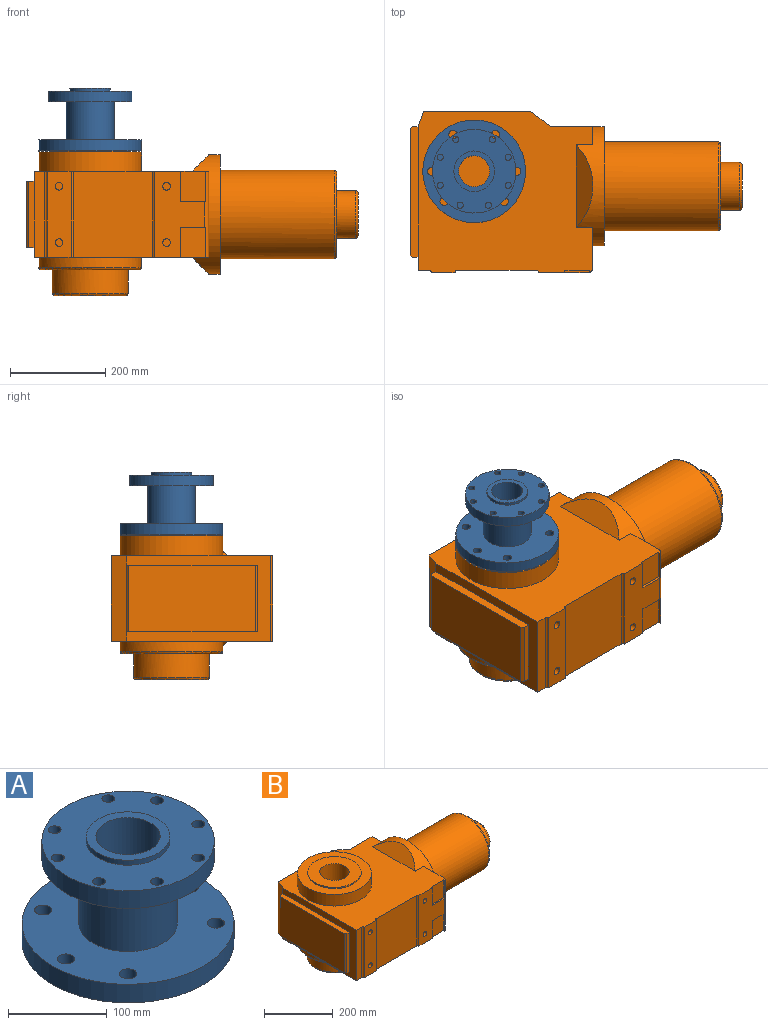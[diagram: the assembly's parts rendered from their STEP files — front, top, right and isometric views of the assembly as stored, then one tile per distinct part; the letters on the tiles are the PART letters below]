
ASSEMBLY  parts=2 mates=1
PART A: 26 faces, bbox 215x215x131 mm
  f0: plane 215x215mm, normal (0,0,-1), area 16235.4mm2, adj f1,f10,f20,f21,f22,f23,f24,f25
  f1: cylinder r=107.5mm len=215mm, axis (0,0,-1), area 15535.2mm2, adj f0,f2
  f2: plane 215x215mm, normal (0,0,1), area 27007.9mm2, adj f1,f3,f20,f21,f22,f23,f24,f25
  f3: cylinder r=50mm len=100mm, axis (0,0,-1), area 25132.7mm2, adj f2,f6
  f4: cylinder r=87.5mm len=175mm, axis (0,0,-1), area 12095.1mm2, adj f5,f6
  f5: plane 175x175mm, normal (0,0,1), area 17316.5mm2, adj f4,f8,f12,f13,f14,f15,f16,f17
  f6: plane 175x175mm, normal (0,0,-1), area 15137mm2, adj f3,f4,f12,f13,f14,f15,f16,f17
  f7: cylinder r=32.5mm len=125mm, axis (0,0,-1), area 25525.4mm2, adj f9,f11
  f8: cylinder r=42.5mm len=85mm, axis (0,0,-1), area 1602.2mm2, adj f5,f9
  f9: plane 85x85mm, normal (0,0,1), area 2356.2mm2, adj f7,f8
  f10: cylinder r=77mm len=154mm, axis (0,0,-1), area 2902.8mm2, adj f0,f11
  f11: plane 154x154mm, normal (0,0,-1), area 15308.2mm2, adj f7,f10
  f12: cylinder r=6.5mm len=22mm, axis (0,0,1), area 898.5mm2, adj f5,f6
  f13: cylinder r=6.5mm len=22mm, axis (0,0,1), area 898.5mm2, adj f5,f6
  f14: cylinder r=6.5mm len=22mm, axis (0,0,1), area 898.5mm2, adj f5,f6
  f15: cylinder r=6.5mm len=22mm, axis (0,0,1), area 898.5mm2, adj f5,f6
  f16: cylinder r=6.5mm len=22mm, axis (0,0,1), area 898.5mm2, adj f5,f6
  f17: cylinder r=6.5mm len=22mm, axis (0,0,1), area 898.5mm2, adj f5,f6
  f18: cylinder r=6.5mm len=22mm, axis (0,0,1), area 898.5mm2, adj f5,f6
  f19: cylinder r=6.5mm len=22mm, axis (0,0,1), area 898.5mm2, adj f5,f6
  f20: cylinder r=8.75mm len=23mm, axis (0,0,-1), area 1264.5mm2, adj f0,f2
  f21: cylinder r=8.75mm len=23mm, axis (0,0,-1), area 1264.5mm2, adj f0,f2
  f22: cylinder r=8.75mm len=23mm, axis (0,0,-1), area 1264.5mm2, adj f0,f2
  f23: cylinder r=8.75mm len=23mm, axis (0,0,-1), area 1264.5mm2, adj f0,f2
  f24: cylinder r=8.75mm len=23mm, axis (0,0,-1), area 1264.5mm2, adj f0,f2
  f25: cylinder r=8.75mm len=23mm, axis (0,0,-1), area 1264.5mm2, adj f0,f2
PART B: 64 faces, bbox 695.5x338x305 mm
  f0: plane 180x84.25mm, normal (1,0,0), area 10413.4mm2, adj f2,f4,f24,f38
  f1: plane 90x38.25mm, normal (1,0,0), area 1066.7mm2, adj f4,f35,f38
  f2: plane 366x338mm, normal (0,0,1), area 76361mm2, adj f0,f3,f5,f6,f7,f8,f9,f11
  f3: plane 224.35x180mm, normal (0,1,0), area 40383mm2, adj f2,f4,f32,f34
  f4: plane 366x338mm, normal (0,0,-1), area 76361mm2, adj f0,f1,f3,f5,f6,f7,f11,f12
  f5: plane 180x103.5mm, normal (0,-1,0), area 12116.9mm2, adj f2,f4,f14,f15,f18,f19,f21,f24
  f6: plane 300.95x180mm, normal (-1,0,0), area 16092mm2, adj f2,f4,f12,f26,f27,f28,f32
  f7: plane 180x50mm, normal (0,-1,0), area 8597.9mm2, adj f2,f4,f22,f23,f48,f50
  f8: plane 90x38.25mm, normal (1,0,0), area 1066.7mm2, adj f2,f35,f38
  f9: cylinder r=107.5mm len=215mm, axis (0,0,-1), area 27693.1mm2, adj f2,f10
  f10: plane 215x215mm, normal (0,0,1), area 17435.8mm2, adj f9,f60
  f11: plane 180x165mm, normal (0,-1,0), area 29700mm2, adj f2,f4,f21,f22
  f12: plane 180x22.5mm, normal (0,-1,0), area 4050mm2, adj f2,f4,f6,f23
  f13: plane 63x4.47mm, normal (-1,0,0), area 281.9mm2, adj f4,f14,f16,f24
  f14: plane 51.7x5mm, normal (0,0,-1), area 257.9mm2, adj f5,f13,f15,f16,f24
  f15: plane 63x5mm, normal (1,0,0), area 315mm2, adj f4,f5,f14,f16
  f16: plane 63x51.7mm, normal (0,-1,0), area 3257.1mm2, adj f4,f13,f14,f15
  f17: plane 63x4.47mm, normal (-1,0,0), area 281.9mm2, adj f2,f19,f20,f24
  f18: plane 63x5mm, normal (1,0,0), area 315mm2, adj f2,f5,f19,f20
  f19: plane 51.7x5mm, normal (0,0,1), area 257.9mm2, adj f5,f17,f18,f20,f24
  f20: plane 63x51.7mm, normal (0,-1,0), area 3257.1mm2, adj f2,f17,f18,f19
  f21: cylinder r=5mm len=180mm, axis (0,0,-1), area 1413.7mm2, adj f2,f4,f5,f11
  f22: cylinder r=5mm len=180mm, axis (0,0,-1), area 1413.7mm2, adj f2,f4,f7,f11
  f23: cylinder r=5mm len=180mm, axis (0,0,-1), area 1413.7mm2, adj f2,f4,f7,f12
  f24: cylinder r=10mm len=180mm, axis (0,0,-1), area 2417mm2, adj f0,f2,f4,f5,f13,f14,f17,f19
  f25: plane 139x12mm, normal (0,1,0), area 1668mm2, adj f26,f28,f33,f36
  f26: plane 274x17mm, normal (0,0,-1), area 4633mm2, adj f6,f25,f27,f29,f33,f36,f37
  f27: plane 139x12mm, normal (0,-1,0), area 1668mm2, adj f6,f26,f28,f37
  f28: plane 274x17mm, normal (0,0,1), area 4633mm2, adj f6,f25,f27,f29,f33,f36,f37
  f29: plane 264x139mm, normal (-1,0,0), area 36696mm2, adj f26,f28,f36,f37
  f30: cylinder r=107.5mm len=215mm, axis (0,0,1), area 14184.3mm2, adj f4,f59
  f31: plane 205x205mm, normal (0,0,-1), area 13150.7mm2, adj f57,f59
  f32: plane 180x32.05mm, normal (-0.94,0.34,0), area 6138.1mm2, adj f2,f3,f4,f6,f33
  f33: plane 139x0.05mm, normal (1,0,0), area 6.8mm2, adj f25,f26,f28,f32
  f34: plane 180x40.8mm, normal (0.62,0.79,0), area 9333.4mm2, adj f2,f3,f4,f35
  f35: plane 180x89.2mm, normal (0,1,0), area 16056mm2, adj f1,f2,f4,f8,f34
  f36: plane 139x5mm, normal (-0.71,0.71,0), area 982.9mm2, adj f25,f26,f28,f29
  f37: plane 139x5mm, normal (-0.71,-0.71,0), area 982.9mm2, adj f26,f27,f28,f29
  f38: cylinder r=125mm len=250mm, axis (-1,0,0), area 23020.6mm2, adj f0,f1,f2,f4,f8,f39,f40,f41
  f39: plane 250x250mm, normal (1,0,0), area 21915.8mm2, adj f38,f42
  f40: plane 173.49x35mm, normal (-0.71,0,0.71), area 5907.3mm2, adj f2,f38
  f41: plane 173.49x35mm, normal (-0.71,0,-0.71), area 5907.3mm2, adj f4,f38
  f42: cylinder r=93mm len=239mm, axis (-1,0,0), area 139656.4mm2, adj f39,f47
  f43: plane 176x176mm, normal (1,0,0), area 16474.5mm2, adj f44,f47
  f44: cylinder r=50mm len=100mm, axis (-1,0,0), area 12566.4mm2, adj f43,f46
  f45: plane 90x90mm, normal (1,0,0), area 6361.7mm2, adj f46
  f46: torus R=45mm, axis (1,0,0), area 2377.7mm2, adj f44,f45
  f47: torus R=88mm, axis (1,0,0), area 4499.7mm2, adj f42,f43
  f48: cylinder r=8mm len=25mm, axis (0,-1,0), area 1256.6mm2, adj f7,f49
  f49: plane 16x16mm, normal (0,-1,0), area 201.1mm2, adj f48
  f50: cylinder r=8mm len=25mm, axis (0,-1,0), area 1256.6mm2, adj f7,f51
  f51: plane 16x16mm, normal (0,-1,0), area 201.1mm2, adj f50
  f52: cylinder r=8mm len=25mm, axis (0,-1,0), area 1256.6mm2, adj f5,f53
  f53: plane 16x16mm, normal (0,-1,0), area 201.1mm2, adj f52
  f54: cylinder r=8mm len=25mm, axis (0,-1,0), area 1256.6mm2, adj f5,f55
  f55: plane 16x16mm, normal (0,-1,0), area 201.1mm2, adj f54
  f56: plane 149x149mm, normal (0,0,-1), area 17436.6mm2, adj f58
  f57: cylinder r=79.5mm len=159mm, axis (0,0,1), area 24476.1mm2, adj f31,f58
  f58: torus R=74.5mm, axis (0,0,-1), area 3833.5mm2, adj f56,f57
  f59: torus R=102.5mm, axis (0,0,-1), area 5215.3mm2, adj f30,f31
  f60: cylinder r=77.5mm len=155mm, axis (0,0,-1), area 1947.8mm2, adj f10,f61
  f61: plane 155x155mm, normal (0,0,1), area 13194.7mm2, adj f60,f63
  f62: plane 85x85mm, normal (0,0,1), area 5674.5mm2, adj f63
  f63: cylinder r=42.5mm len=251mm, axis (0,0,1), area 67025.9mm2, adj f61,f62
PLACE A t=(-35.45,66.03,-43.35)mm
PLACE B t=(25.56,0.85,-86.35)mm fixed
MATE revolute B.f9 <-> A.f3  axis (0,0,-1) through (-35.45,66.03,-43.35)mm
